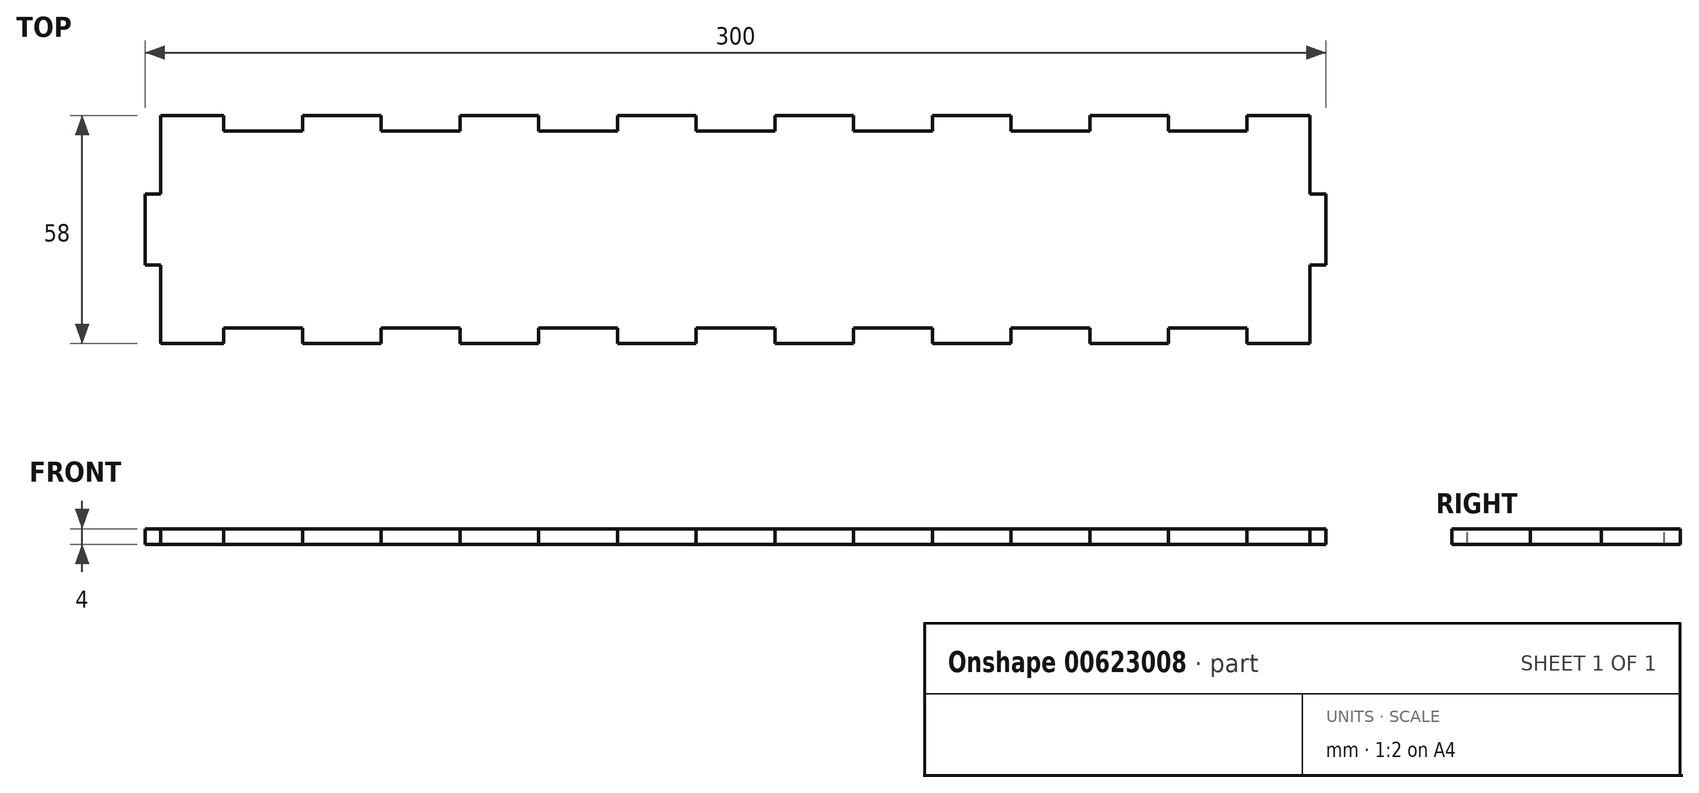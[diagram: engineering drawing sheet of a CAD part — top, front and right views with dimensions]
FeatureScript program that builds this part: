
annotation { "Feature Type Name" : "Feature", "Feature Type Description" : "" }
export const myFeature = defineFeature(function(context is Context, id is Id, definition is map)
    precondition{}
    {
        {
            var Q0;
            Q0=qCreatedBy(makeId("Top.planeOp"),FACE);
            var sketch = newSketch(context, id + "F0", { "sketchPlane" : qUnion([Q0])});
            skLineSegment(sketch, "E0.bottom", {"start": v(0, 0) * mm, "end": v(-300, 0) * mm});
            skLineSegment(sketch, "E0.top", {"start": v(0, 58) * mm, "end": v(-300, 58) * mm});
            skLineSegment(sketch, "E0.left", {"start": v(0, 0) * mm, "end": v(0, 58) * mm});
            skLineSegment(sketch, "E0.right", {"start": v(-300, 0) * mm, "end": v(-300, 58) * mm});
            skSolve(sketch);
        }
        {
            var Q0;
            Q0 = qSketchRegion(id + "F0", true);
            extrude(context, id + "F1", {"entities" : qUnion([Q0]), "depth" : 4 * mm, "offsetDistance" : 25 * mm});
        }
        {
            var Q0;
            Q0=makeQuery(id+"F1.opExtrude","CAP_FACE",FACE,{"disambiguationData":[OSD([sQuery(id+"F0.wireOp",EDGE,"E0.bottom"),sQuery(id+"F0.wireOp",EDGE,"E0.top"),sQuery(id+"F0.wireOp",EDGE,"E0.left"),sQuery(id+"F0.wireOp",EDGE,"E0.right")])],"isStart":false});
            var sketch = newSketch(context, id + "F2", { "sketchPlane" : qUnion([Q0])});
            skLineSegment(sketch, "E1.bottom", {"start": v(-280, 0) * mm, "end": v(-260, 0) * mm});
            skLineSegment(sketch, "E1.top", {"start": v(-280, 4) * mm, "end": v(-260, 4) * mm});
            skLineSegment(sketch, "E1.left", {"start": v(-280, 0) * mm, "end": v(-280, 4) * mm});
            skLineSegment(sketch, "E1.right", {"start": v(-260, 0) * mm, "end": v(-260, 4) * mm});
            skLineSegment(sketch, "E2.bottom", {"start": v(-160, 0) * mm, "end": v(-140, 0) * mm});
            skLineSegment(sketch, "E2.top", {"start": v(-160, 4) * mm, "end": v(-140, 4) * mm});
            skLineSegment(sketch, "E2.left", {"start": v(-160, 0) * mm, "end": v(-160, 4) * mm});
            skLineSegment(sketch, "E2.right", {"start": v(-140, 0) * mm, "end": v(-140, 4) * mm});
            skLineSegment(sketch, "E3.bottom", {"start": v(-120, 0) * mm, "end": v(-100, 0) * mm});
            skLineSegment(sketch, "E3.top", {"start": v(-120, 4) * mm, "end": v(-100, 4) * mm});
            skLineSegment(sketch, "E3.left", {"start": v(-120, 0) * mm, "end": v(-120, 4) * mm});
            skLineSegment(sketch, "E3.right", {"start": v(-100, 0) * mm, "end": v(-100, 4) * mm});
            skLineSegment(sketch, "E4.bottom", {"start": v(-80, 0) * mm, "end": v(-60, 0) * mm});
            skLineSegment(sketch, "E4.top", {"start": v(-80, 4) * mm, "end": v(-60, 4) * mm});
            skLineSegment(sketch, "E4.left", {"start": v(-80, 0) * mm, "end": v(-80, 4) * mm});
            skLineSegment(sketch, "E4.right", {"start": v(-60, 0) * mm, "end": v(-60, 4) * mm});
            skLineSegment(sketch, "E5.bottom", {"start": v(-40, 0) * mm, "end": v(-20, 0) * mm});
            skLineSegment(sketch, "E5.top", {"start": v(-40, 4) * mm, "end": v(-20, 4) * mm});
            skLineSegment(sketch, "E5.left", {"start": v(-40, 0) * mm, "end": v(-40, 4) * mm});
            skLineSegment(sketch, "E5.right", {"start": v(-20, 0) * mm, "end": v(-20, 4) * mm});
            skLineSegment(sketch, "E6.bottom", {"start": v(-240, 0) * mm, "end": v(-220, 0) * mm});
            skLineSegment(sketch, "E6.top", {"start": v(-240, 4) * mm, "end": v(-220, 4) * mm});
            skLineSegment(sketch, "E6.left", {"start": v(-240, 0) * mm, "end": v(-240, 4) * mm});
            skLineSegment(sketch, "E6.right", {"start": v(-220, 0) * mm, "end": v(-220, 4) * mm});
            skLineSegment(sketch, "E7.bottom", {"start": v(-200, 0) * mm, "end": v(-180, 0) * mm});
            skLineSegment(sketch, "E7.top", {"start": v(-200, 4) * mm, "end": v(-180, 4) * mm});
            skLineSegment(sketch, "E7.left", {"start": v(-200, 0) * mm, "end": v(-200, 4) * mm});
            skLineSegment(sketch, "E7.right", {"start": v(-180, 0) * mm, "end": v(-180, 4) * mm});
            skLineSegment(sketch, "E8.bottom", {"start": v(-280, 58) * mm, "end": v(-260, 58) * mm});
            skLineSegment(sketch, "E8.top", {"start": v(-280, 54) * mm, "end": v(-260, 54) * mm});
            skLineSegment(sketch, "E8.left", {"start": v(-280, 58) * mm, "end": v(-280, 54) * mm});
            skLineSegment(sketch, "E8.right", {"start": v(-260, 58) * mm, "end": v(-260, 54) * mm});
            skLineSegment(sketch, "E9.bottom", {"start": v(-240, 58) * mm, "end": v(-220, 58) * mm});
            skLineSegment(sketch, "E9.top", {"start": v(-240, 54) * mm, "end": v(-220, 54) * mm});
            skLineSegment(sketch, "E9.left", {"start": v(-240, 58) * mm, "end": v(-240, 54) * mm});
            skLineSegment(sketch, "E9.right", {"start": v(-220, 58) * mm, "end": v(-220, 54) * mm});
            skLineSegment(sketch, "E10.bottom", {"start": v(-200, 58) * mm, "end": v(-180, 58) * mm});
            skLineSegment(sketch, "E10.top", {"start": v(-200, 54) * mm, "end": v(-180, 54) * mm});
            skLineSegment(sketch, "E10.left", {"start": v(-200, 58) * mm, "end": v(-200, 54) * mm});
            skLineSegment(sketch, "E10.right", {"start": v(-180, 58) * mm, "end": v(-180, 54) * mm});
            skLineSegment(sketch, "E11.bottom", {"start": v(-160, 58) * mm, "end": v(-140, 58) * mm});
            skLineSegment(sketch, "E11.top", {"start": v(-160, 54) * mm, "end": v(-140, 54) * mm});
            skLineSegment(sketch, "E11.left", {"start": v(-160, 58) * mm, "end": v(-160, 54) * mm});
            skLineSegment(sketch, "E11.right", {"start": v(-140, 58) * mm, "end": v(-140, 54) * mm});
            skLineSegment(sketch, "E12.bottom", {"start": v(-120, 58) * mm, "end": v(-100, 58) * mm});
            skLineSegment(sketch, "E12.top", {"start": v(-120, 54) * mm, "end": v(-100, 54) * mm});
            skLineSegment(sketch, "E12.left", {"start": v(-120, 58) * mm, "end": v(-120, 54) * mm});
            skLineSegment(sketch, "E12.right", {"start": v(-100, 58) * mm, "end": v(-100, 54) * mm});
            skLineSegment(sketch, "E13.bottom", {"start": v(-80, 58) * mm, "end": v(-60, 58) * mm});
            skLineSegment(sketch, "E13.top", {"start": v(-80, 54) * mm, "end": v(-60, 54) * mm});
            skLineSegment(sketch, "E13.left", {"start": v(-80, 58) * mm, "end": v(-80, 54) * mm});
            skLineSegment(sketch, "E13.right", {"start": v(-60, 58) * mm, "end": v(-60, 54) * mm});
            skLineSegment(sketch, "E14.bottom", {"start": v(-40, 58.3) * mm, "end": v(-20, 58.3) * mm});
            skLineSegment(sketch, "E14.top", {"start": v(-40, 54) * mm, "end": v(-20, 54) * mm});
            skLineSegment(sketch, "E14.left", {"start": v(-40, 58.3) * mm, "end": v(-40, 54) * mm});
            skLineSegment(sketch, "E14.right", {"start": v(-20, 58.3) * mm, "end": v(-20, 54) * mm});
            skLineSegment(sketch, "E15.bottom", {"start": v(0, 58) * mm, "end": v(-4, 58) * mm});
            skLineSegment(sketch, "E15.top", {"start": v(0, 38) * mm, "end": v(-4, 38) * mm});
            skLineSegment(sketch, "E15.left", {"start": v(0, 58) * mm, "end": v(0, 38) * mm});
            skLineSegment(sketch, "E15.right", {"start": v(-4, 58) * mm, "end": v(-4, 38) * mm});
            skLineSegment(sketch, "E16.bottom", {"start": v(0, 0) * mm, "end": v(-4, 0) * mm});
            skLineSegment(sketch, "E16.top", {"start": v(0, 20) * mm, "end": v(-4, 20) * mm});
            skLineSegment(sketch, "E16.left", {"start": v(0, 0) * mm, "end": v(0, 20) * mm});
            skLineSegment(sketch, "E16.right", {"start": v(-4, 0) * mm, "end": v(-4, 20) * mm});
            skLineSegment(sketch, "E17.bottom", {"start": v(-300, 58) * mm, "end": v(-296, 58) * mm});
            skLineSegment(sketch, "E17.top", {"start": v(-300, 38) * mm, "end": v(-296, 38) * mm});
            skLineSegment(sketch, "E17.left", {"start": v(-300, 58) * mm, "end": v(-300, 38) * mm});
            skLineSegment(sketch, "E17.right", {"start": v(-296, 58) * mm, "end": v(-296, 38) * mm});
            skLineSegment(sketch, "E18.bottom", {"start": v(-300, 0) * mm, "end": v(-296, 0) * mm});
            skLineSegment(sketch, "E18.top", {"start": v(-300, 20) * mm, "end": v(-296, 20) * mm});
            skLineSegment(sketch, "E18.left", {"start": v(-300, 0) * mm, "end": v(-300, 20) * mm});
            skLineSegment(sketch, "E18.right", {"start": v(-296, 0) * mm, "end": v(-296, 20) * mm});
            skSolve(sketch);
        }
        {
            var Q0;
            Q0 = qSketchRegion(id + "F2", true);
            extrude(context, id + "F3", {"entities" : qUnion([Q0]), "operationType" : NewBodyOperationType.REMOVE, "oppositeDirection" : true, "depth" : 4 * mm, "offsetDistance" : 25 * mm});
        }
    });
